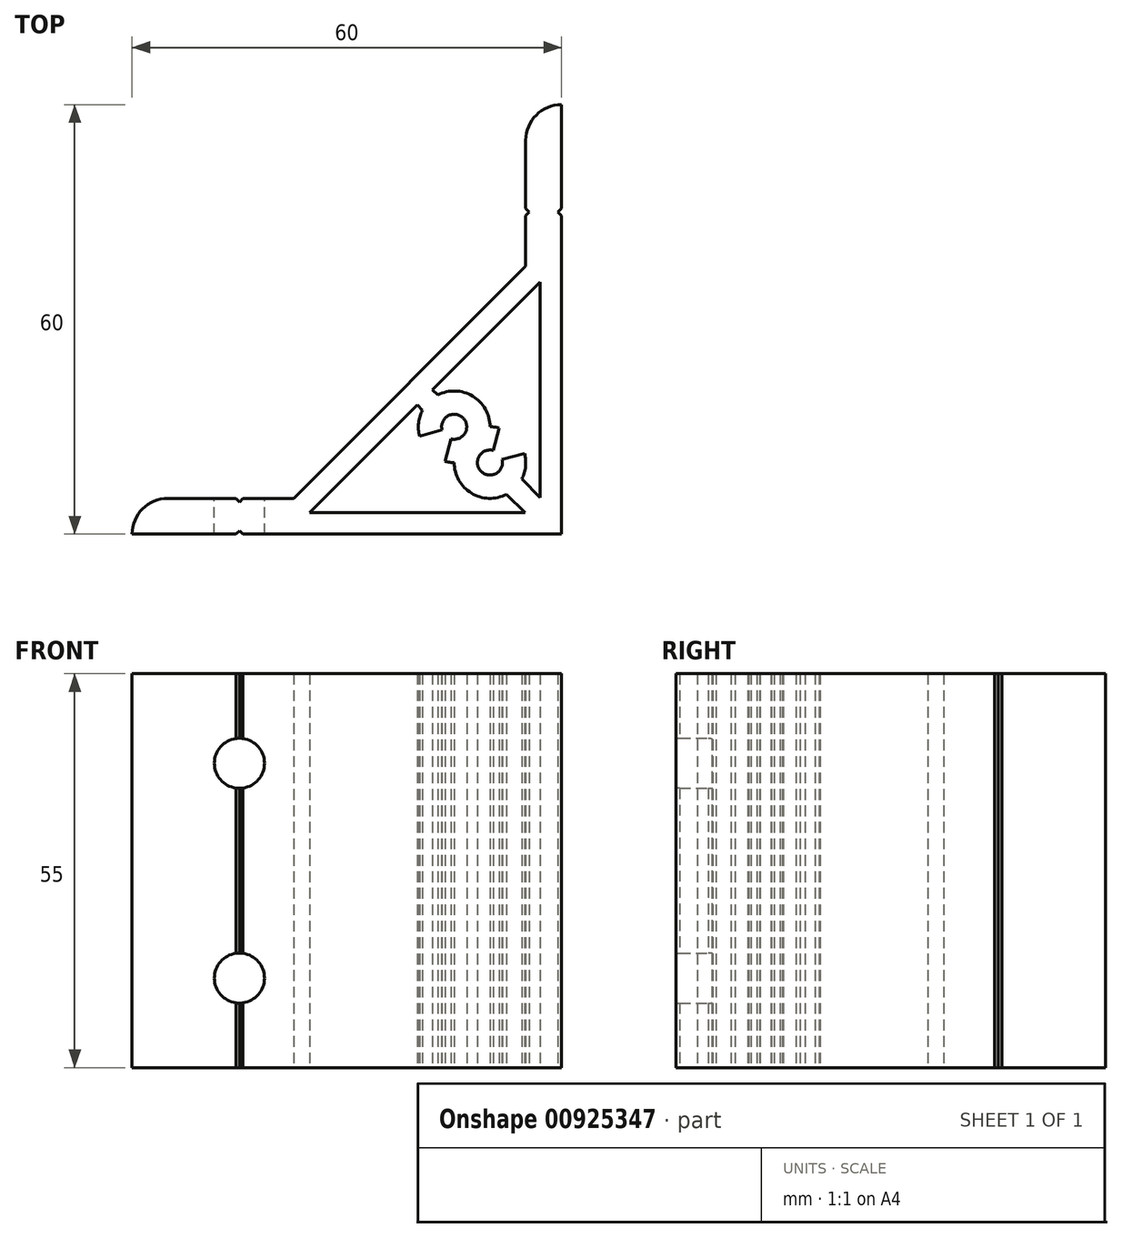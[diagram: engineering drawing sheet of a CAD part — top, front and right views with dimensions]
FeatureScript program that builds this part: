
annotation { "Feature Type Name" : "Feature", "Feature Type Description" : "" }
export const myFeature = defineFeature(function(context is Context, id is Id, definition is map)
    precondition{}
    {
        {
            var Q0;
            Q0=qCreatedBy(makeId("Top.planeOp"),FACE);
            var sketch = newSketch(context, id + "F0", { "sketchPlane" : qUnion([Q0])});
            skLineSegment(sketch, "E0", {"start": v(-23.13, -24.22) * mm, "end": v(-30.2, -24.22) * mm});
            skLineSegment(sketch, "E1", {"start": v(9.3, 25.78) * mm, "end": v(9.3, 16.28) * mm});
            skLineSegment(sketch, "E2", {"start": v(14.3, -29.22) * mm, "end": v(-30.2, -29.22) * mm});
            skLineSegment(sketch, "E3", {"start": v(14.3, 15.28) * mm, "end": v(14.3, -29.22) * mm});
            skLineSegment(sketch, "E4", {"start": v(9.3, 15.28) * mm, "end": v(9.3, 8.2) * mm});
            skLineSegment(sketch, "E5", {"start": v(14.3, 30.78) * mm, "end": v(14.3, 16.28) * mm});
            skLineSegment(sketch, "E6", {"start": v(-31.2, -24.22) * mm, "end": v(-40.7, -24.22) * mm});
            skLineSegment(sketch, "E7", {"start": v(-31.2, -29.22) * mm, "end": v(-45.7, -29.22) * mm});
            skLineSegment(sketch, "E8", {"start": v(-30.2, -24.22) * mm, "end": v(-30.7, -24.72) * mm});
            skLineSegment(sketch, "E9", {"start": v(-30.7, -24.72) * mm, "end": v(-31.2, -24.22) * mm});
            skLineSegment(sketch, "E10", {"start": v(14.3, 15.28) * mm, "end": v(13.8, 15.78) * mm});
            skLineSegment(sketch, "E11", {"start": v(13.8, 15.78) * mm, "end": v(14.3, 16.28) * mm});
            skLineSegment(sketch, "E12", {"start": v(9.8, 15.78) * mm, "end": v(9.3, 15.28) * mm});
            skLineSegment(sketch, "E13", {"start": v(9.3, 16.28) * mm, "end": v(9.8, 15.78) * mm});
            skLineSegment(sketch, "E14", {"start": v(-31.2, -29.22) * mm, "end": v(-30.7, -28.72) * mm});
            skLineSegment(sketch, "E15", {"start": v(-30.7, -28.72) * mm, "end": v(-30.2, -29.22) * mm});
            skLineSegment(sketch, "E16", {"start": v(-5.54, -15.52) * mm, "end": v(-2.4, -14.68) * mm});
            skLineSegment(sketch, "E17", {"start": v(-1.16, -15.91) * mm, "end": v(-2, -19.05) * mm});
            skLineSegment(sketch, "E18", {"start": v(9.12, -17.93) * mm, "end": v(5.98, -18.77) * mm});
            skLineSegment(sketch, "E19", {"start": v(4.75, -17.53) * mm, "end": v(5.59, -14.4) * mm});
            skArc(sketch, "E20", {"start": v(-2, -19.05) * mm, "mid": v(-1.36, -19.18) * mm, "end": v(-0.7, -19.22) * mm});
            skArc(sketch, "E21", {"start": v(-1.16, -15.91) * mm, "mid": v(0.53, -12.99) * mm, "end": v(-2.4, -14.68) * mm});
            skArc(sketch, "E22", {"start": v(5.59, -14.4) * mm, "mid": v(4.94, -14.27) * mm, "end": v(4.3, -14.22) * mm});
            skArc(sketch, "E23", {"start": v(4.75, -17.53) * mm, "mid": v(3.05, -20.46) * mm, "end": v(5.98, -18.77) * mm});
            skLineSegment(sketch, "E24", {"start": v(-20.9, -26.22) * mm, "end": v(-5.86, -11.2) * mm});
            skLineSegment(sketch, "E25", {"start": v(-5.86, -11.2) * mm, "end": v(-5.14, -11.91) * mm});
            skArc(sketch, "E26", {"start": v(-5.14, -11.91) * mm, "mid": v(-5.68, -13.68) * mm, "end": v(-5.54, -15.52) * mm});
            skArc(sketch, "E27", {"start": v(-0.7, -19.22) * mm, "mid": v(1.7, -23.5) * mm, "end": v(6.6, -23.66) * mm});
            skLineSegment(sketch, "E28", {"start": v(6.6, -23.66) * mm, "end": v(9.17, -26.22) * mm});
            skLineSegment(sketch, "E29", {"start": v(9.17, -26.22) * mm, "end": v(-20.9, -26.22) * mm});
            skLineSegment(sketch, "E30", {"start": v(11.3, -24.1) * mm, "end": v(8.73, -21.54) * mm});
            skArc(sketch, "E31", {"start": v(8.73, -21.54) * mm, "mid": v(9.26, -19.77) * mm, "end": v(9.12, -17.93) * mm});
            skArc(sketch, "E32", {"start": v(4.3, -14.22) * mm, "mid": v(1.88, -9.95) * mm, "end": v(-3.02, -9.79) * mm});
            skLineSegment(sketch, "E33", {"start": v(-3.02, -9.79) * mm, "end": v(-3.74, -9.07) * mm});
            skLineSegment(sketch, "E34", {"start": v(-3.74, -9.07) * mm, "end": v(11.3, 5.96) * mm});
            skLineSegment(sketch, "E35", {"start": v(11.3, 5.96) * mm, "end": v(11.3, -24.1) * mm});
            skArc(sketch, "E36", {"start": v(-40.7, -24.22) * mm, "mid": v(-44.24, -25.69) * mm, "end": v(-45.7, -29.22) * mm});
            skArc(sketch, "E37", {"start": v(14.3, 30.78) * mm, "mid": v(10.76, 29.31) * mm, "end": v(9.3, 25.78) * mm});
            skLineSegment(sketch, "E38", {"start": v(-23.13, -24.22) * mm, "end": v(9.3, 8.2) * mm});
            skSolve(sketch);
        }
        {
            var Q0;
            Q0 = qSketchRegion(id + "F0", true);
            extrude(context, id + "F1", {"entities" : qUnion([Q0]), "depth" : 55 * mm, "offsetDistance" : 25 * mm});
        }
        {
            var Q0;
            Q0=makeQuery(id+"F1.opExtrude","SWEPT_FACE",FACE,{"disambiguationData":[OSD([sQuery(id+"F0.wireOp",EDGE,"E0")])]});
            var sketch = newSketch(context, id + "F2", { "sketchPlane" : qUnion([Q0])});
            skLineSegment(sketch, "E39.0", {"start": v(30.7, 55) * mm, "end": v(30.7, 0) * mm, "construction": true});
            skPoint(sketch, "E40", {"position": v(30.7, 12.5) * mm});
            skPoint(sketch, "E41", {"position": v(30.7, 42.5) * mm});
            skSolve(sketch);
        }
        {
            var Q0;
            Q0=sQuery(id+"F2.wireOp",VERTEX,"E41");
            var Q1;
            Q1=sQuery(id+"F2.wireOp",VERTEX,"E40");
            var Q2;
            Q2=makeQuery(id+"F1.opExtrude","SWEPT_BODY",BODY,{"disambiguationData":[OSD([sQuery(id+"F0.wireOp",EDGE,"E0"),sQuery(id+"F0.wireOp",EDGE,"E1"),sQuery(id+"F0.wireOp",EDGE,"E2"),sQuery(id+"F0.wireOp",EDGE,"E3"),sQuery(id+"F0.wireOp",EDGE,"E4"),sQuery(id+"F0.wireOp",EDGE,"E5"),sQuery(id+"F0.wireOp",EDGE,"E6"),sQuery(id+"F0.wireOp",EDGE,"E7"),sQuery(id+"F0.wireOp",EDGE,"E8"),sQuery(id+"F0.wireOp",EDGE,"E9"),sQuery(id+"F0.wireOp",EDGE,"E10"),sQuery(id+"F0.wireOp",EDGE,"E11"),sQuery(id+"F0.wireOp",EDGE,"E12"),sQuery(id+"F0.wireOp",EDGE,"E13"),sQuery(id+"F0.wireOp",EDGE,"E14"),sQuery(id+"F0.wireOp",EDGE,"E15"),sQuery(id+"F0.wireOp",EDGE,"E16"),sQuery(id+"F0.wireOp",EDGE,"E17"),sQuery(id+"F0.wireOp",EDGE,"E18"),sQuery(id+"F0.wireOp",EDGE,"E19"),sQuery(id+"F0.wireOp",EDGE,"E20"),sQuery(id+"F0.wireOp",EDGE,"E21"),sQuery(id+"F0.wireOp",EDGE,"E22"),sQuery(id+"F0.wireOp",EDGE,"E23"),sQuery(id+"F0.wireOp",EDGE,"E24"),sQuery(id+"F0.wireOp",EDGE,"E25"),sQuery(id+"F0.wireOp",EDGE,"E26"),sQuery(id+"F0.wireOp",EDGE,"E27"),sQuery(id+"F0.wireOp",EDGE,"E28"),sQuery(id+"F0.wireOp",EDGE,"E29"),sQuery(id+"F0.wireOp",EDGE,"E30"),sQuery(id+"F0.wireOp",EDGE,"E31"),sQuery(id+"F0.wireOp",EDGE,"E32"),sQuery(id+"F0.wireOp",EDGE,"E33"),sQuery(id+"F0.wireOp",EDGE,"E34"),sQuery(id+"F0.wireOp",EDGE,"E35"),sQuery(id+"F0.wireOp",EDGE,"E36"),sQuery(id+"F0.wireOp",EDGE,"E37"),sQuery(id+"F0.wireOp",EDGE,"E38")])]});
            hole(context, id + "F3", {"style" : HoleStyle.SIMPLE, "endStyle" : HoleEndStyle.BLIND, "standardTappedOrClearance" : lookupTablePath({ "standard" : "ISO", "size" : "7", "type" : "Drilled" }), "standardBlindInLast" : lookupTablePath({ "standard" : "ISO", "size" : "7", "type" : "Drilled" }), "holeDiameter" : 7 * mm, "majorDiameter" : 5 * mm, "holeDepth" : 5 * mm, "isTappedThrough" : true, "tappedDepth" : 9 * mm, "tapClearance" : 3, "startFromSketch" : true, "locations" : qUnion([Q0, Q1]), "scope" : qUnion([Q2])});
        }
        {
            var Q0;
            Q0=makeQuery(id+"F1.opExtrude","CAP_EDGE",EDGE,{"disambiguationData":[OSD([sQuery(id+"F0.wireOp",EDGE,"E38")])],"isStart":true});
            cPoint(context, id + "F4", {"entities" : qUnion([Q0]), "parameter" : 0.5});
        }
        {
            var Q0;
            Q0=makeQuery(id+"F1.opExtrude","CAP_EDGE",EDGE,{"disambiguationData":[OSD([sQuery(id+"F0.wireOp",EDGE,"E38")])],"isStart":false});
            cPoint(context, id + "F5", {"entities" : qUnion([Q0]), "parameter" : 0.5});
        }
        {
            var Q0;
            Q0=makeQuery(id+"F1.opExtrude","CAP_VERTEX",VERTEX,{"disambiguationData":[OSD([sQuery(id+"F0.wireOp",EDGE,"E2"),sQuery(id+"F0.wireOp",EDGE,"E3")])],"isStart":true});
            var Q1;
            Q1 = qCreatedBy(id + "F4" ,VERTEX);
            var Q2;
            Q2 = qCreatedBy(id + "F5" ,VERTEX);
            cPlane(context, id + "F6", {"entities" : qUnion([Q0, Q1, Q2]), "cplaneType" : CPlaneType.THREE_POINT, "offset" : 25 * mm, "width" : 150 * mm, "height" : 150 * mm});
        }
    });
